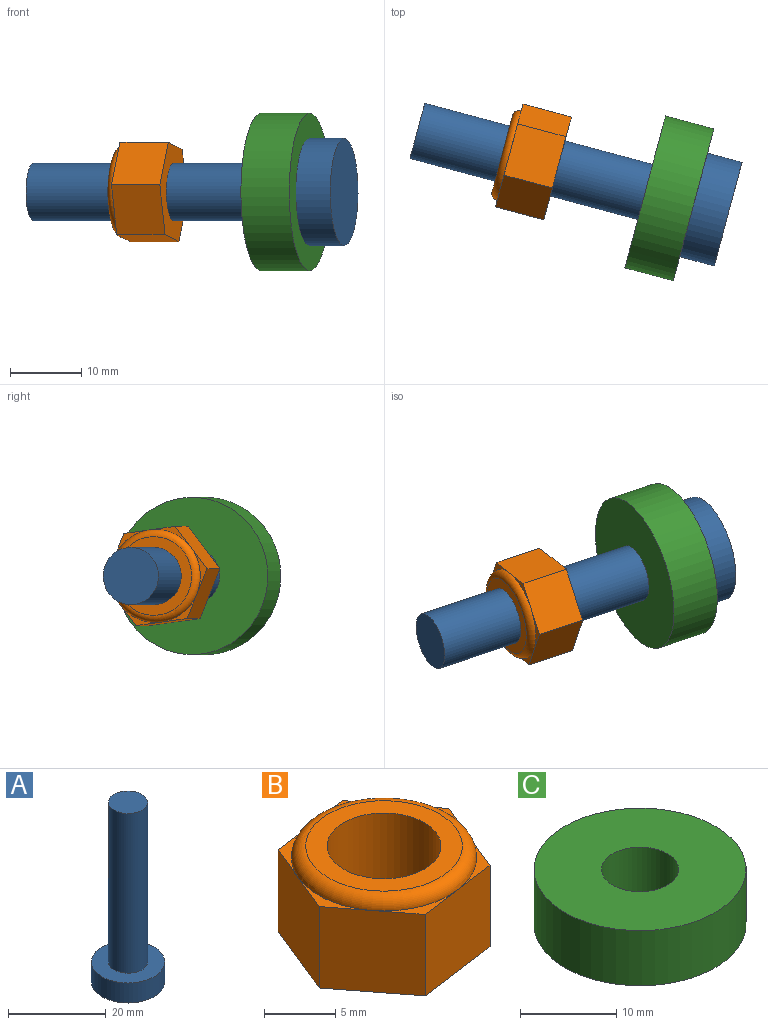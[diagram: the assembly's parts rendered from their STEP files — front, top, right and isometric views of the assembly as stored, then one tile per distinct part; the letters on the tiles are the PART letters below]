
ASSEMBLY  parts=3 mates=2
PART A: 5 faces, bbox 15x15x45 mm
  f0: cylinder r=4mm len=40mm, axis (0,0,-1), area 1005.3mm2, adj f1,f4
  f1: plane 8x8mm, normal (0,0,1), area 50.3mm2, adj f0
  f2: cylinder r=7.5mm len=15mm, axis (0,0,1), area 235.6mm2, adj f3,f4
  f3: plane 15x15mm, normal (0,0,-1), area 176.7mm2, adj f2
  f4: plane 15x15mm, normal (0,0,1), area 126.4mm2, adj f0,f2
PART B: 16 faces, bbox 14.9x14.1x8 mm
  f0: plane 7x6.94mm, normal (-0.92,0.38,0), area 52.5mm2, adj f1,f2,f8,f11,f14
  f1: plane 7x5.94mm, normal (-0.79,-0.61,0), area 52.5mm2, adj f0,f4,f8,f10,f14
  f2: plane 7.44x7mm, normal (-0.13,0.99,0), area 52.5mm2, adj f0,f3,f8,f11,f13
  f3: plane 7x5.94mm, normal (0.79,0.61,0), area 52.5mm2, adj f2,f5,f8,f9,f13
  f4: plane 7.44x7mm, normal (0.13,-0.99,0), area 52.5mm2, adj f1,f5,f8,f10,f12
  f5: plane 7x6.94mm, normal (0.92,-0.38,0), area 52.5mm2, adj f3,f4,f8,f9,f12
  f6: cylinder r=4mm len=8mm, axis (0,0,-1), area 201.1mm2, adj f7,f8
  f7: plane 11x11mm, normal (0,0,1), area 44.8mm2, adj f6,f15
  f8: plane 14.88x13.88mm, normal (0,0,-1), area 96.1mm2, adj f0,f1,f2,f3,f4,f5,f6
  f9: plane 6.44x2.29mm, normal (0,0,1), area 2.3mm2, adj f3,f5,f15
  f10: plane 6.01x2.97mm, normal (0,0,1), area 2.3mm2, adj f1,f4,f15
  f11: plane 5.15x3.97mm, normal (0,0,1), area 2.3mm2, adj f0,f2,f15
  f12: plane 5.15x3.97mm, normal (0,0,1), area 2.3mm2, adj f4,f5,f15
  f13: plane 6.01x2.97mm, normal (0,0,1), area 2.3mm2, adj f2,f3,f15
  f14: plane 6.44x2.29mm, normal (0,0,1), area 2.3mm2, adj f0,f1,f15
  f15: torus R=5.5mm, axis (0,0,1), area 60.6mm2, adj f7,f9,f10,f11,f12,f13,f14
PART C: 4 faces, bbox 22x22x7 mm
  f0: cylinder r=4mm len=8mm, axis (0,0,-1), area 175.9mm2, adj f2,f3
  f1: cylinder r=11mm len=22mm, axis (0,0,-1), area 483.8mm2, adj f2,f3
  f2: plane 22x22mm, normal (0,0,1), area 329.9mm2, adj f0,f1
  f3: plane 22x22mm, normal (0,0,-1), area 329.9mm2, adj f0,f1
PLACE A rot(axis=(-0.13,-0.98,-0.13),91deg) t=(65.43,-38.78,-33.47)mm
PLACE B rot(axis=(-0.68,-0.52,0.52),111.8deg) t=(62.67,27.03,-123.91)mm
PLACE C rot(axis=(-0.68,-0.52,0.52),111.8deg) t=(72.11,-13.84,-95.06)mm
MATE cylindrical B.f6 <-> A.f0  axis (0.97,-0.26,0) through (39.46,-28.66,-91.25)mm
MATE cylindrical C.f0 <-> A.f0  axis (0.97,-0.26,0) through (59.46,-34.02,-91.25)mm
